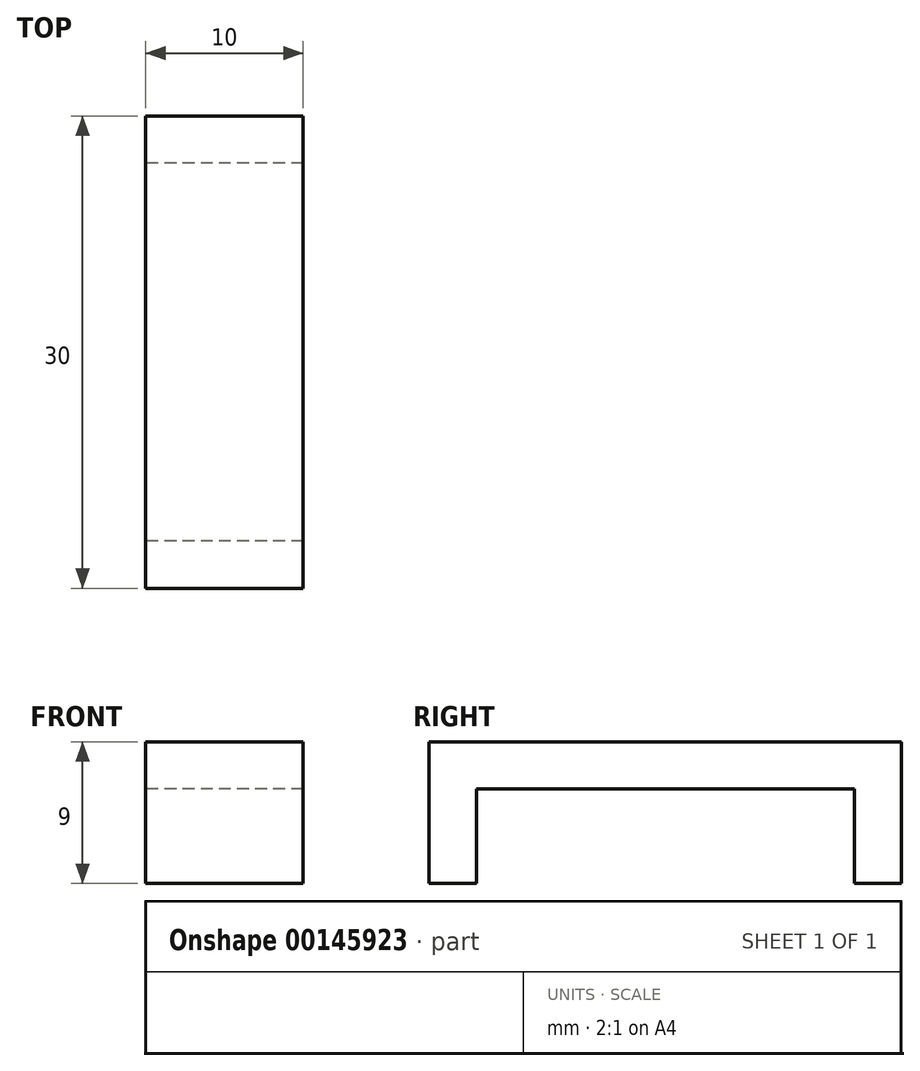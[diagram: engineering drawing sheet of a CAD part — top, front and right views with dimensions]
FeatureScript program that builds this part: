
annotation { "Feature Type Name" : "Feature", "Feature Type Description" : "" }
export const myFeature = defineFeature(function(context is Context, id is Id, definition is map)
    precondition{}
    {
        {
            var Q0;
            Q0=qCreatedBy(makeId("Right.planeOp"),FACE);
            var sketch = newSketch(context, id + "F0", { "sketchPlane" : qUnion([Q0])});
            skLineSegment(sketch, "E0.bottom", {"start": v(-15, 0) * mm, "end": v(-12, 0) * mm});
            skLineSegment(sketch, "E0.top", {"start": v(-15, 9) * mm, "end": v(-12, 9) * mm});
            skLineSegment(sketch, "E0.left", {"start": v(-15, 0) * mm, "end": v(-15, 9) * mm});
            skLineSegment(sketch, "E0.right", {"start": v(-12, 0) * mm, "end": v(-12, 9) * mm});
            skLineSegment(sketch, "E1.bottom", {"start": v(-12, 9) * mm, "end": v(0, 9) * mm});
            skLineSegment(sketch, "E1.top", {"start": v(-12, 6) * mm, "end": v(0, 6) * mm});
            skLineSegment(sketch, "E1.left", {"start": v(-12, 9) * mm, "end": v(-12, 6) * mm});
            skLineSegment(sketch, "E1.right", {"start": v(0, 9) * mm, "end": v(0, 6) * mm});
            skLineSegment(sketch, "E2.MirrorCS", {"start": v(12, 9) * mm, "end": v(12, 6) * mm});
            skLineSegment(sketch, "E3.MirrorCS", {"start": v(15, 0) * mm, "end": v(12, 0) * mm});
            skLineSegment(sketch, "E4.MirrorCS", {"start": v(15, 9) * mm, "end": v(12, 9) * mm});
            skLineSegment(sketch, "E5.MirrorCS", {"start": v(15, 0) * mm, "end": v(15, 9) * mm});
            skLineSegment(sketch, "E6.MirrorCS", {"start": v(12, 0) * mm, "end": v(12, 9) * mm});
            skLineSegment(sketch, "E7.MirrorCS", {"start": v(12, 6) * mm, "end": v(0, 6) * mm});
            skLineSegment(sketch, "E8.MirrorCS", {"start": v(12, 9) * mm, "end": v(0, 9) * mm});
            skSolve(sketch);
        }
        {
            var Q0;
            Q0 = qSketchRegion(id + "F0", true);
            extrude(context, id + "F1", {"entities" : qUnion([Q0]), "depth" : 10 * mm});
        }
    });
